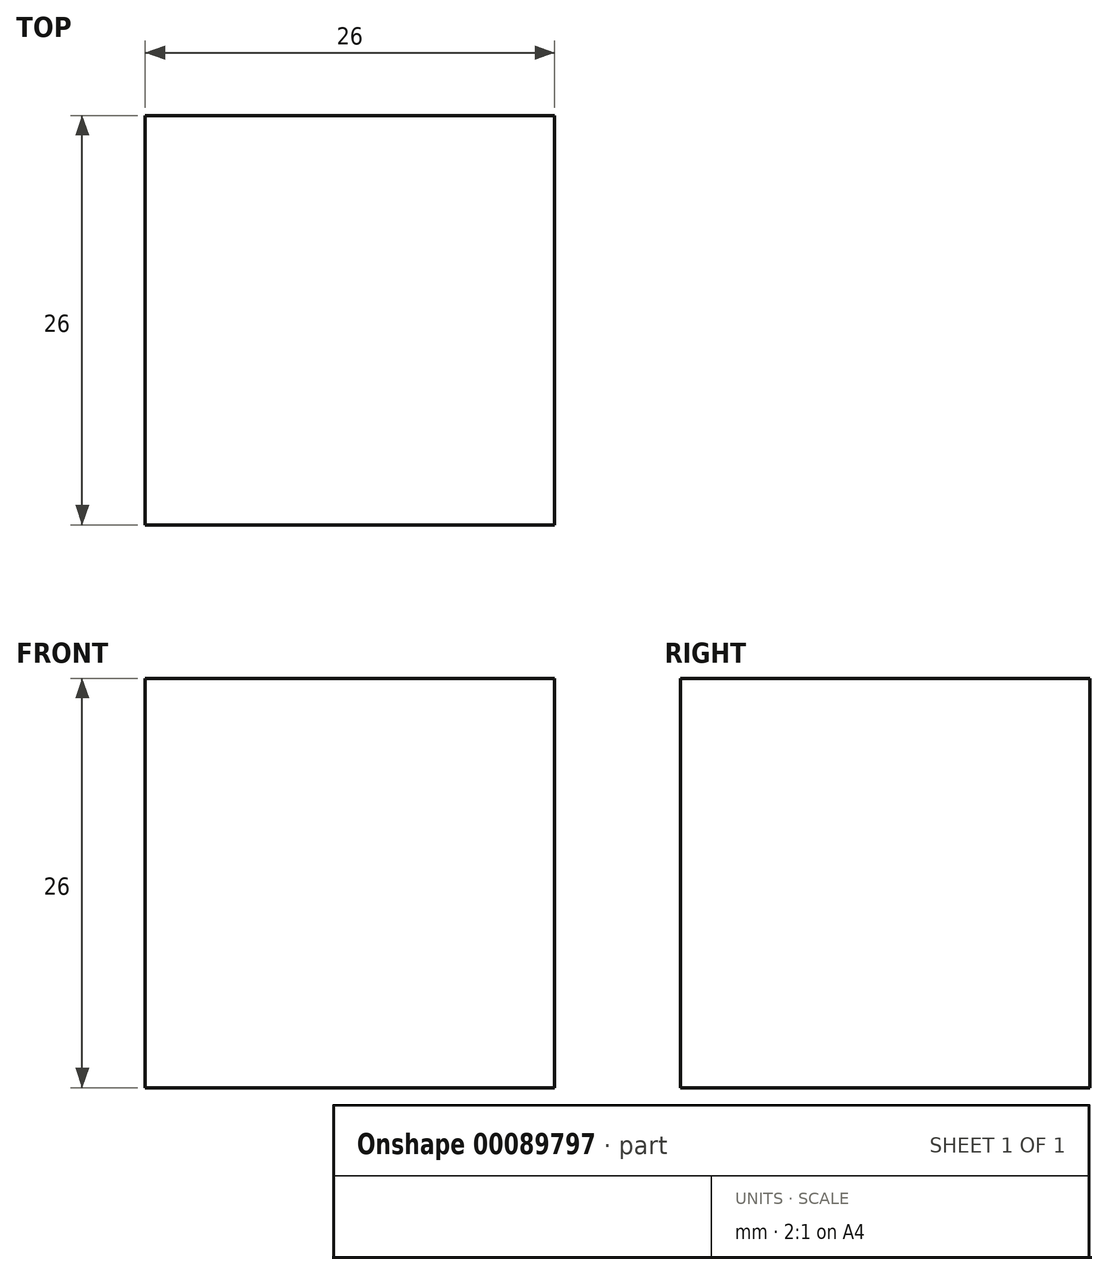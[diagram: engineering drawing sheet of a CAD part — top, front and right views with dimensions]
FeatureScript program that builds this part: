
annotation { "Feature Type Name" : "Feature", "Feature Type Description" : "" }
export const myFeature = defineFeature(function(context is Context, id is Id, definition is map)
    precondition{}
    {
        {
            var Q0;
            Q0=qCreatedBy(makeId("Front.planeOp"),FACE);
            var sketch = newSketch(context, id + "F0", { "sketchPlane" : qUnion([Q0])});
            skLineSegment(sketch, "E0.bottom", {"start": v(0, 0) * mm, "end": v(26, 0) * mm});
            skLineSegment(sketch, "E0.top", {"start": v(0, 26) * mm, "end": v(26, 26) * mm});
            skLineSegment(sketch, "E0.left", {"start": v(0, 0) * mm, "end": v(0, 26) * mm});
            skLineSegment(sketch, "E0.right", {"start": v(26, 0) * mm, "end": v(26, 26) * mm});
            skSolve(sketch);
        }
        {
            var Q0;
            Q0=makeQuery(id+"F0.imprint","IMPRINT",FACE,{"disambiguationData":[TD([[makeQuery(id+"F0.imprint","IMPRINT",EDGE,{"derivedFrom":sQuery(id+"F0.wireOp",EDGE,"E0.bottom")}),1.0]])]});
            extrude(context, id + "F1", {"entities" : qUnion([Q0]), "depth" : 26 * mm});
        }
    });
